# Revit family: Doorset_Exterior Door High Security with Escape Route Terminal_ASSA ABLOY DE_Hardware Light
name_source: partatom
category: Doors
revit_build: Autodesk Revit 2015 (Build: 20140606_1530(x64)
units: mm (PartAtom-declared; Revit-internal decimal feet)

## types (7) — shared parameters
Architectural Accessory = 1x Lead cover_10314_Effeff
Architectural Hardware = 1x Handle (inside) + Knob (outside)_OneSystem_ASSA ABLOY
BIMobject Brand = ASSA ABLOY DE
BIMobject Instructions Video = https://www.youtube.com
BIMobject Product Family = Exterior Door Solutions
BIMobject Product Group = Single-Steel/Aluminium-Self Closing-Access Control-Escape Route
BIMobject Product Page = http://bimobject.com
BIMobject Unique ref = ES1-AC-ML-ET-HS-DC-DE07
Date of publishing = 22.09.2016
Description = Self Closing Exterior Door with Access Control
Door Closers = 1x Door Closer DC700 with guide rail_Cam-Motion®_ASSA ABLOY
Edition number = 1
Electronic Accessories_1 = 1x IO-Module_OneSystem_ASSA ABLOY
Electronic Accessories_2 = 1x Power Supply_1003_Effeff
Electronic Accessories_3 = 1x Power Supply_SCALA_Effeff
Electronic Accessories_4 = 1x Cable__ASSA ABLOY
Frame Material = Steel/Aluminium
Function = Exterior
Hardware Set = ES1-AC-ML-ET-HS-DC-DE07
IFC Classification = Door
Identity and Access Solutions_1 = 1x SCALAnet Software_SCALA_Effeff
Identity and Access Solutions_2 = 1x SCALAnet Controller_SCALA_Effeff
Identity and Access Solutions_3 = 1x SCALA Reader (inside)_SCALA_Effeff
Identity and Access Solutions_4 = 1x SCALA Reader (outside)_SCALA_Effeff
Locksets = 1x Motor multiple locking _OneSystem_ASSA ABLOY
Manufacturer = ASSA ABLOY
Maximum Door Height = 3750 mm
Maximum Door Width = 1500 mm
Maximum Thickness = 105 mm
Minimum Door Height = 2110 mm
Minimum Door Width = 900 mm
Minimum Thickness = 38 mm
Model = Doorset_Entrance Door High Security with Escape Route Terminal_ASSA ABLOY DE_Hardware Light
NBS Reference Code = 59-23
NBS Reference Description = Doorsets
Name = Entrance Door High Security with Escape Route Terminal
OmniClass Number = 23-17 11 00
OmniClass Title = Doors
Panel Material = Steel/Aluminium
Panic and Exit Devices_1 = 1x Control Device_720-40_effeff
Panic and Exit Devices_2 = 1x Control Terminal_Flush-mounted 1380-15_Effeff
Product Guid = b5c892cf-2a41-4025-b72d-0596e90751de
Provider = ASSA ABLOY DE
Strikes, Magnetic Locks and Bolts = 1x Escape Route Strike_331U80_Effeff
Thickness = 90 mm
Thickness Constraint = 90 mm
URL = http://www.assaabloy.de
Uniclass 1.4 Code = L411
Uniclass 1.4 Description = Doors
Uniclass 2.0 Code = PR-59-23
Uniclass 2.0 Description = Doorsets
Wall Closure = By host

## per-type parameters (varying)
| type | Frame Height | Frame Width | Height | Panel Height | Panel Width | Rough Height | Rough Width | Width |
| 900 x 2110 mm (1000 x 2160 mm) | 2160 mm | 1000 mm | 2160 mm | 2110 mm | 900 mm | 2172 mm  [stored 7.12598 ft] | 1024 mm  [stored 3.35958 ft] | 1000 mm |
| 1000 x 2500 mm (1100 x 2550 mm) | 2550 mm | 1100 mm | 2550 mm | 2500 mm | 1000 mm | 2562 mm | 1124 mm | 1100 mm |
| 1000 x 2110 mm (1100 x 2160 mm) | 2160 mm | 1100 mm | 2160 mm | 2110 mm | 1000 mm | 2172 mm  [stored 7.12598 ft] | 1124 mm | 1100 mm |
| 1000 x 3750 mm (1100 x 3800 mm) | 3800 mm | 1100 mm | 3800 mm | 3750 mm | 1000 mm | 3812 mm | 1124 mm | 1100 mm |
| 1300 x 2500 mm (1400 x 2550 mm) | 2550 mm | 1400 mm | 2550 mm | 2500 mm | 1300 mm | 2562 mm | 1424 mm | 1400 mm |
| 1300 x 3750 mm (1400 x 3800 mm) | 3800 mm | 1400 mm | 3800 mm | 3750 mm | 1300 mm | 3812 mm | 1424 mm | 1400 mm |
| 1500 x 3750 mm (1600 x 3800 mm) | 3800 mm | 1600 mm | 3800 mm | 3750 mm | 1500 mm | 3812 mm | 1624 mm | 1600 mm |

note: column(s) folded — value = type name in every type: Type Comments

note: [stored X ft] marks values corroborated as IEEE doubles in the binary element streams (Revit-internal decimal feet)

## geometry (parser evidence)
native form markers: Blend x8, Sweep x3
no freeform markers — native parametric forms only
